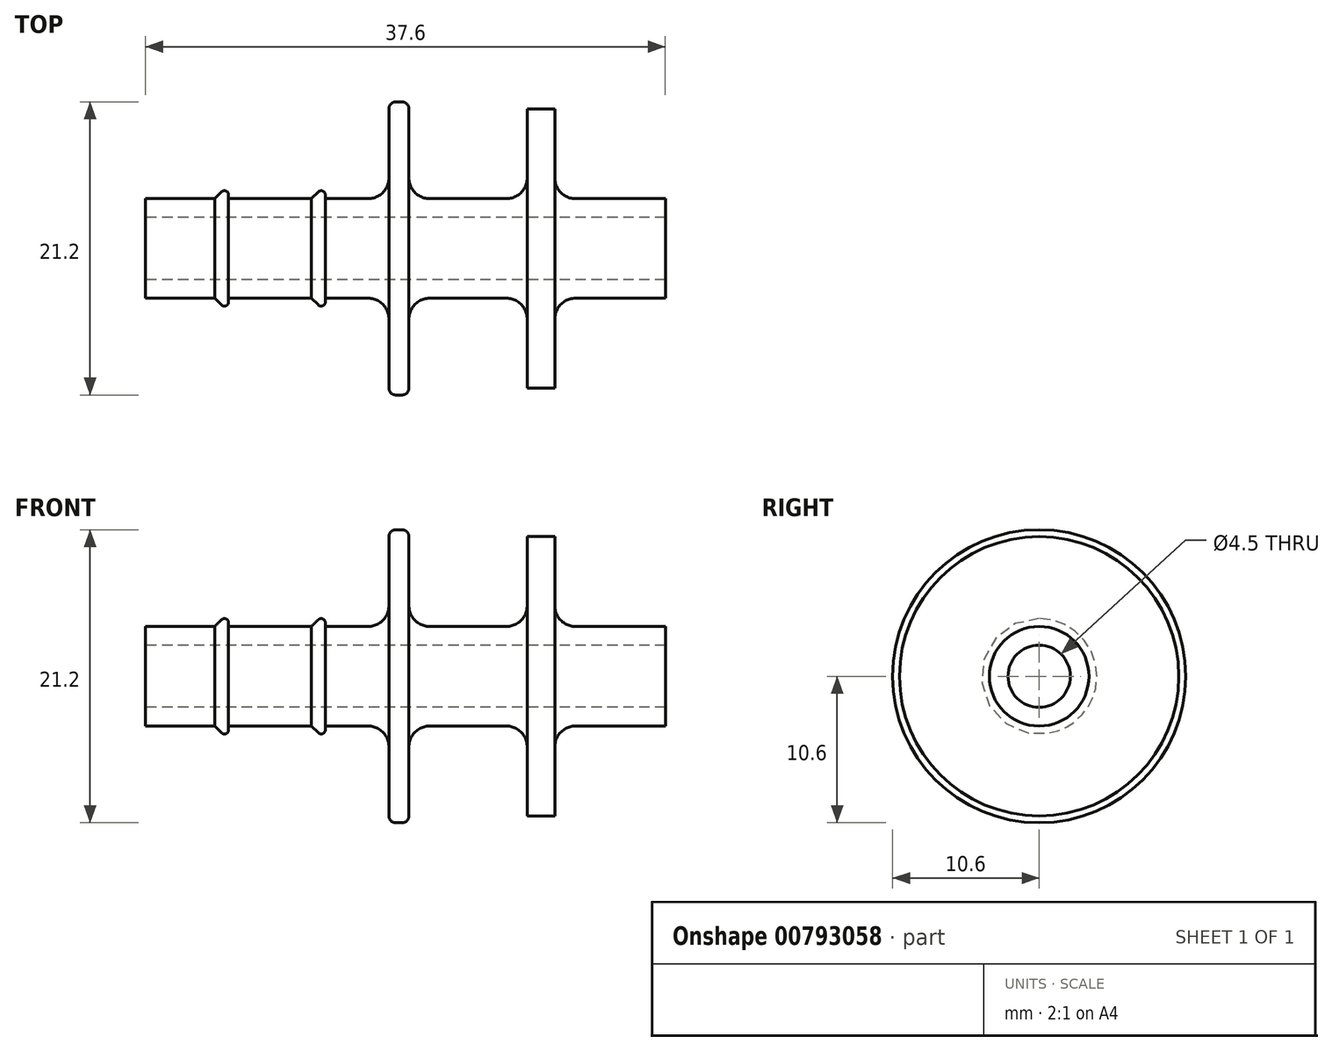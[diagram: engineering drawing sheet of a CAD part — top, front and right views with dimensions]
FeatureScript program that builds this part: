
annotation { "Feature Type Name" : "Feature", "Feature Type Description" : "" }
export const myFeature = defineFeature(function(context is Context, id is Id, definition is map)
    precondition{}
    {
        {
            var Q0;
            Q0=qCreatedBy(makeId("Front.planeOp"),FACE);
            var sketch = newSketch(context, id + "F0", { "sketchPlane" : qUnion([Q0])});
            skLineSegment(sketch, "E0", {"start": v(-19.2, -2.25) * mm, "end": v(18.4, -2.25) * mm});
            skLineSegment(sketch, "E1", {"start": v(18.4, -2.25) * mm, "end": v(18.4, -3.6) * mm});
            skLineSegment(sketch, "E2", {"start": v(18.4, -3.6) * mm, "end": v(11.9, -3.6) * mm});
            skLineSegment(sketch, "E3", {"start": v(10.4, -5.1) * mm, "end": v(10.4, -10.1) * mm});
            skLineSegment(sketch, "E4", {"start": v(10.4, -10.1) * mm, "end": v(8.4, -10.1) * mm});
            skLineSegment(sketch, "E5", {"start": v(8.4, -10.1) * mm, "end": v(8.4, -5.1) * mm});
            skLineSegment(sketch, "E6", {"start": v(6.9, -3.6) * mm, "end": v(1.34, -3.6) * mm});
            skLineSegment(sketch, "E7", {"start": v(-0.16, -5.1) * mm, "end": v(-0.16, -10.1) * mm});
            skLineSegment(sketch, "E8", {"start": v(-0.66, -10.6) * mm, "end": v(-1.1, -10.6) * mm});
            skLineSegment(sketch, "E9", {"start": v(-1.6, -10.1) * mm, "end": v(-1.6, -5.1) * mm});
            skLineSegment(sketch, "E10", {"start": v(-3.1, -3.6) * mm, "end": v(-6.2, -3.6) * mm});
            skLineSegment(sketch, "E11", {"start": v(-7.2, -3.6) * mm, "end": v(-13.2, -3.6) * mm});
            skLineSegment(sketch, "E12", {"start": v(-19.2, -2.25) * mm, "end": v(-19.2, -3.6) * mm});
            skLineSegment(sketch, "E13", {"start": v(-19.2, -3.6) * mm, "end": v(-14.2, -3.6) * mm});
            skPoint(sketch, "E14.visualSharp", {"position": v(10.4, -3.6) * mm});
            skArc(sketch, "E14.filletArc", {"start": v(11.9, -3.6) * mm, "mid": v(10.83, -4.04) * mm, "end": v(10.4, -5.1) * mm});
            skPoint(sketch, "E15.visualSharp", {"position": v(8.4, -3.6) * mm});
            skArc(sketch, "E15.filletArc", {"start": v(8.4, -5.1) * mm, "mid": v(7.95, -4.04) * mm, "end": v(6.9, -3.6) * mm});
            skPoint(sketch, "E16.visualSharp", {"position": v(-1.6, -3.6) * mm});
            skArc(sketch, "E16.filletArc", {"start": v(-1.6, -5.1) * mm, "mid": v(-2.05, -4.04) * mm, "end": v(-3.1, -3.6) * mm});
            skPoint(sketch, "E17.visualSharp", {"position": v(-0.16, -3.6) * mm});
            skArc(sketch, "E17.filletArc", {"start": v(1.34, -3.6) * mm, "mid": v(0.28, -4.04) * mm, "end": v(-0.16, -5.1) * mm});
            skLineSegment(sketch, "E18", {"start": v(-7.2, -3.6) * mm, "end": v(-6.72, -4.09) * mm});
            skLineSegment(sketch, "E19", {"start": v(-6.2, -3.88) * mm, "end": v(-6.2, -3.6) * mm});
            skPoint(sketch, "E20.visualSharp", {"position": v(-6.2, -4.6) * mm});
            skArc(sketch, "E20.filletArc", {"start": v(-6.72, -4.09) * mm, "mid": v(-6.4, -4.15) * mm, "end": v(-6.2, -3.88) * mm});
            skLineSegment(sketch, "E21", {"start": v(-14.2, -3.6) * mm, "end": v(-13.72, -4.09) * mm});
            skLineSegment(sketch, "E22", {"start": v(-13.2, -3.88) * mm, "end": v(-13.2, -3.6) * mm});
            skPoint(sketch, "E23.visualSharp", {"position": v(-13.2, -4.6) * mm});
            skArc(sketch, "E23.filletArc", {"start": v(-13.72, -4.09) * mm, "mid": v(-13.4, -4.15) * mm, "end": v(-13.2, -3.88) * mm});
            skPoint(sketch, "E24.visualSharp", {"position": v(-0.16, -10.6) * mm});
            skArc(sketch, "E24.filletArc", {"start": v(-0.66, -10.6) * mm, "mid": v(-0.3, -10.45) * mm, "end": v(-0.16, -10.1) * mm});
            skPoint(sketch, "E25.visualSharp", {"position": v(-1.6, -10.6) * mm});
            skArc(sketch, "E25.filletArc", {"start": v(-1.6, -10.1) * mm, "mid": v(-1.46, -10.45) * mm, "end": v(-1.1, -10.6) * mm});
            skLineSegment(sketch, "E26", {"start": v(-19.25, 0) * mm, "end": v(18.35, 0) * mm});
            skSolve(sketch);
        }
        {
            var Q0;
            Q0 = qSketchRegion(id + "F0", true);
            var Q1;
            Q1=sQuery(id+"F0.wireOp",EDGE,"E26");
            revolve(context, id + "F1", {"surfaceOperationType" : NewSurfaceOperationType.NEW, "entities" : qUnion([Q0]), "axis" : qUnion([Q1]), "revolveType" : RevolveType.FULL});
        }
    });
